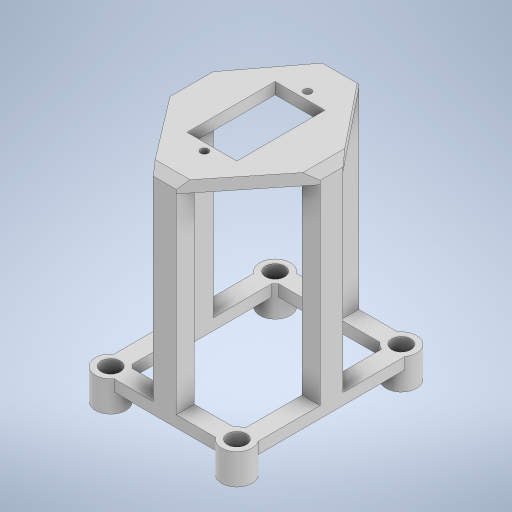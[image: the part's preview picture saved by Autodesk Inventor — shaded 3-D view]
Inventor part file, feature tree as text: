
AUTODESK INVENTOR PART (.ipt)
format: ipt  version: 2024.2 (Build 282272000, 272)  size: 406,016 bytes
history: native  units: mm
features: extrude x5, sketch x5, chamfer x1
ambient origin geometry x8: Origin, YZ Plane, XZ Plane, XY Plane, X Axis, Y Axis, Z Axis, Center Point
bodies: Solid1 (feature_tree)
feature tree (11):
  extrude  "Extrusion1"  Depth=5.0mm
  extrude  "Extrusion2"  Depth=5.0mm
  extrude  "Extrusion3"  Depth=8.0mm
  extrude  "Extrusion4"  Depth=8.0mm
  extrude  "Extrusion5"  Depth=4.0mm
  chamfer  "Chamfer1"  Distance=4.0mm
  sketch  "Sketch1"  dims[d0=5.0mm d1=5.0mm]
  sketch  "Sketch2"  dims[d2=5.0mm d3=5.0mm]
  sketch  "Sketch3"  dims[d4=8.0mm d5=8.0mm]
  sketch  "Sketch4"  dims[d6=8.0mm d7=8.0mm]
  sketch  "Sketch5"  dims[d8=4.0mm d9=4.0mm d10=4.0mm d11=4.0mm d12=4.0mm d13=4.0mm d18=43.0mm d23=33.0mm d24=4.7mm d25=4.7mm d26=4.7mm d27=4.7mm d28=2.35mm d29=2.35mm d30=4.0mm d31=2.35mm d32=3.0mm d33=0.0mm d34=5.0mm d35=8.0mm d37=8.0mm d38=5.0mm d39=5.0mm d40=5.0mm d41=5.0mm d42=0.0mm d43=6.0mm d44=6.0mm d45=6.0mm d46=6.0mm d47=18.5mm d48=18.5mm d49=13.5mm d50=13.5mm d51=50.0mm d52=0.0mm d53=23.0mm d54=13.0mm d55=10.0mm d56=10.0mm d68=10.0mm d69=23.0mm d70=10.0mm d71=3.0mm d72=0.0mm d73=2.0mm d74=2.0mm d75=6.5mm d76=6.5mm d77=2.0mm d78=2.0mm d79=3.0mm d80=0.0mm d81=2.0mm d82=2.0mm d83=45.0deg]
